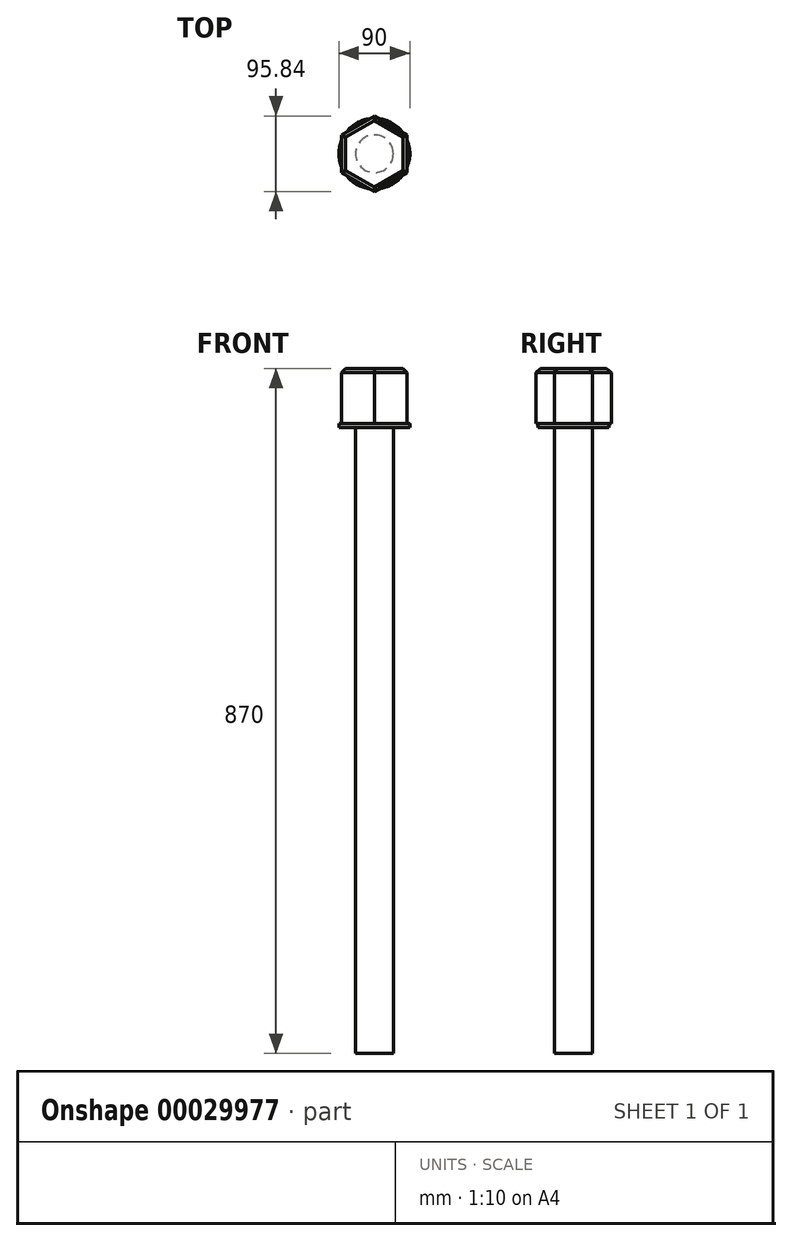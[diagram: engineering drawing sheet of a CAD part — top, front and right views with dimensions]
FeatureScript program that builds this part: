
annotation { "Feature Type Name" : "Feature", "Feature Type Description" : "" }
export const myFeature = defineFeature(function(context is Context, id is Id, definition is map)
    precondition{}
    {
        {
            var Q0;
            Q0=qCreatedBy(makeId("Top.planeOp"),FACE);
            var sketch = newSketch(context, id + "F0", { "sketchPlane" : qUnion([Q0])});
            skCircle(sketch, "E0.cCircle", {"center": v(0, 0) * mm, "radius": 41.5 * mm, "construction": true});
            skLineSegment(sketch, "E0.0", {"start": v(41.5, -23.96) * mm, "end": v(0, -47.92) * mm});
            skLineSegment(sketch, "E0.1", {"start": v(0, -47.92) * mm, "end": v(-41.5, -23.96) * mm});
            skLineSegment(sketch, "E0.2", {"start": v(-41.5, -23.96) * mm, "end": v(-41.5, 23.96) * mm});
            skLineSegment(sketch, "E0.3", {"start": v(-41.5, 23.96) * mm, "end": v(0, 47.92) * mm});
            skLineSegment(sketch, "E0.4", {"start": v(0, 47.92) * mm, "end": v(41.5, 23.96) * mm});
            skLineSegment(sketch, "E0.5", {"start": v(41.5, 23.96) * mm, "end": v(41.5, -23.96) * mm});
            skPoint(sketch, "E0.0.midPoint", {"position": v(20.75, -35.94) * mm});
            skLineSegment(sketch, "E1", {"start": v(0, 0) * mm, "end": v(0, 68.6) * mm, "construction": true});
            skLineSegment(sketch, "E2", {"start": v(0, 0) * mm, "end": v(82.26, 0) * mm, "construction": true});
            skSolve(sketch);
        }
        {
            var Q0;
            Q0 = qSketchRegion(id + "F0", true);
            extrude(context, id + "F1", {"entities" : qUnion([Q0]), "oppositeDirection" : true, "depth" : 70 * mm});
        }
        {
            var Q0;
            Q0=makeQuery(id+"F1.opExtrude","CAP_EDGE",EDGE,{"disambiguationData":[OSD([sQuery(id+"F0.wireOp",EDGE,"E0.1")])],"isStart":true});
            var Q1;
            Q1=makeQuery(id+"F1.opExtrude","CAP_EDGE",EDGE,{"disambiguationData":[OSD([sQuery(id+"F0.wireOp",EDGE,"E0.2")])],"isStart":true});
            var Q2;
            Q2=makeQuery(id+"F1.opExtrude","CAP_EDGE",EDGE,{"disambiguationData":[OSD([sQuery(id+"F0.wireOp",EDGE,"E0.3")])],"isStart":true});
            var Q3;
            Q3=makeQuery(id+"F1.opExtrude","CAP_EDGE",EDGE,{"disambiguationData":[OSD([sQuery(id+"F0.wireOp",EDGE,"E0.4")])],"isStart":true});
            var Q4;
            Q4=makeQuery(id+"F1.opExtrude","CAP_EDGE",EDGE,{"disambiguationData":[OSD([sQuery(id+"F0.wireOp",EDGE,"E0.5")])],"isStart":true});
            var Q5;
            Q5=makeQuery(id+"F1.opExtrude","CAP_EDGE",EDGE,{"disambiguationData":[OSD([sQuery(id+"F0.wireOp",EDGE,"E0.0")])],"isStart":true});
            chamfer(context, id + "F2", {"entities" : qUnion([Q0, Q1, Q2, Q3, Q4, Q5]), "width" : 5 * mm, "tangentPropagation" : true});
        }
        {
            var Q0;
            Q0=makeQuery(id+"F1.opExtrude","CAP_FACE",FACE,{"disambiguationData":[OSD([sQuery(id+"F0.wireOp",EDGE,"E0.0"),sQuery(id+"F0.wireOp",EDGE,"E0.1"),sQuery(id+"F0.wireOp",EDGE,"E0.2"),sQuery(id+"F0.wireOp",EDGE,"E0.3"),sQuery(id+"F0.wireOp",EDGE,"E0.4"),sQuery(id+"F0.wireOp",EDGE,"E0.5")])],"isStart":false});
            var sketch = newSketch(context, id + "F3", { "sketchPlane" : qUnion([Q0])});
            skCircle(sketch, "E3", {"center": v(0, 0) * mm, "radius": 45 * mm});
            skSolve(sketch);
        }
        {
            var Q0;
            Q0 = qSketchRegion(id + "F3", true);
            extrude(context, id + "F4", {"entities" : qUnion([Q0]), "operationType" : NewBodyOperationType.ADD, "depth" : 5 * mm});
        }
        {
            var Q0;
            Q0=makeQuery(id+"F4.opExtrude","CAP_FACE",FACE,{"disambiguationData":[OSD([sQuery(id+"F3.wireOp",EDGE,"E3")])],"isStart":false});
            var sketch = newSketch(context, id + "F5", { "sketchPlane" : qUnion([Q0])});
            skCircle(sketch, "E4", {"center": v(0, 0) * mm, "radius": 24 * mm});
            skSolve(sketch);
        }
        {
            var Q0;
            Q0 = qSketchRegion(id + "F5", true);
            extrude(context, id + "F6", {"entities" : qUnion([Q0]), "operationType" : NewBodyOperationType.ADD, "depth" : 795 * mm});
        }
    });
